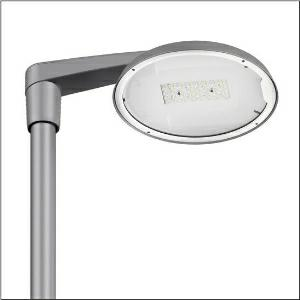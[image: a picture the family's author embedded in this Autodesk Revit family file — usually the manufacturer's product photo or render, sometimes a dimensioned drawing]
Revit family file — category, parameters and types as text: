
# Revit family: dl_50_iq_mini___st0_5a_5xa248b41f08he_b68c
name_source: partatom
category: Lighting Fixtures
units: mm (PartAtom-declared; Revit-internal decimal feet)

## family parameters
Cut with Voids When Loaded = No
Host = Face
Light Source = No
Part Type = Normal
Room Calculation Point = No
Round Connector Dimension = Use Diameter
Shared = No

## types (1)
- --- (1 x LED, 9400 lm, 64.6 W, 4000K)
    Apparent Load = 65 VA
    CIE Flux Codes = 41 75 97 100 100
    Color Rendering = 70
    Color Temperature = 4000K
    Default Elevation = 1800 mm
    Description = DL 50 iQ mini, mast luminaire, primary light control with lens, of PMMA, primary optical cover: cover, of toughened safety glass, transparent, light distribution: ST0.5a, light emission: direct distribution, primary light characteristic: asymmetric, installation type: side-entry, post-top, LED, High Power LED, rated luminous flux: 9.400lm, luminous efficacy: 146lm/W, light colour: 740, colour temperature: 4000K, control gear: iQ Street-Remote, control: optimised constant luminous flux control (CLO 2.0), Desk-Remote (wireless, voltage-free reading and setting of iQ features in the workshop via application-optimized NFC function/RFID function), Light-Fading, Smart-Wire, Night-Set, Lumen-Switch, Temp-Guard, Auto-Match, Street-Remote, mains connection: 230..240V, AC, 50/60Hz, connection cable pre-assembled, cable length: 8,5m, start of lifetime: 65W, end of service life: 68W, reduction: 29W, luminaire housing, of diecast aluminium, powder-coated, SITECO metallic grey (DB 702S), inclination adjustable: 0°, 5°, 10° (post-top) | 0°, -5°, -10°, -15° (side-entry), please order mast post-top element or mast side-entry element separately, diameter: 500mm, height: 115mm, post-top: for spigot size d x l = 76 x 100mm; with reducer (optional accessory) 60 x 100mm | side-entry: for spigot size d x l = 60 x 100mm; with reducer (optional accessory) 42 x 100mm, mounting height: 4..6m, protection rating (complete): IP66, insulation class (complete): insulation class II (safety insulation), certification: CE, ENEC, ENEC+, VDE, impact resistance: IK08, permissible operating ambient temperature for outdoor applications: -25..+40°C, standard-compliant lighting for roads and squares, packaging unit: 1 piece

Light Distribution: ST0.5a
    Height = 115 mm
    Lamp = 1 x LED
    Lamp Light Flux = 9400 lm
    Lamp Power = 64.6 W
    Lamp count = 1
    Length = 500 mm
    Luminous efficacy = 146 lm/W
    Manufacturer = Siteco
    ModVariant = No
    Model = 5XA248B41F08HE
    Number of Poles = 1
    OnlyDefault = Yes
    Power Factor = 1
    Product Name = DL 50 iQ mini | ST0.5a
    Product group = mast luminaire | pylon top
    ProductGroupID = 6100
    Protection Class = Protection class II
    Protection Degree = IP 66
    RLX_Detail_Level = 1
    RLX_Emergency_Light_Flux = 0 lm
    RLX_Emergency_Type = 0
    RLX_Emergency_Type_DB = No
    RlxData = <blob elided: 126705 chars, md5=e13874b0>
    Socket = socket
    Standby Power = 0 W
    System Light Flux = 9400 lm
    System Power = 65 W
    Type Comments = factory setting: luminous flux: 100 % | dim-lin: 254 | 655 mA
    Type Image = l_1251794.jpg
    URL = http://relux.com
    VarID = @adj_142681
    Voltage = 0 V
    Weight = 0.00 kg
    Width = 0 mm  [stored 0 ft]

note: [stored X ft] marks values corroborated as IEEE doubles in the binary element streams (Revit-internal decimal feet)

## geometry (parser evidence)
native form markers: Blend x4, Sweep x10
no freeform markers — native parametric forms only
